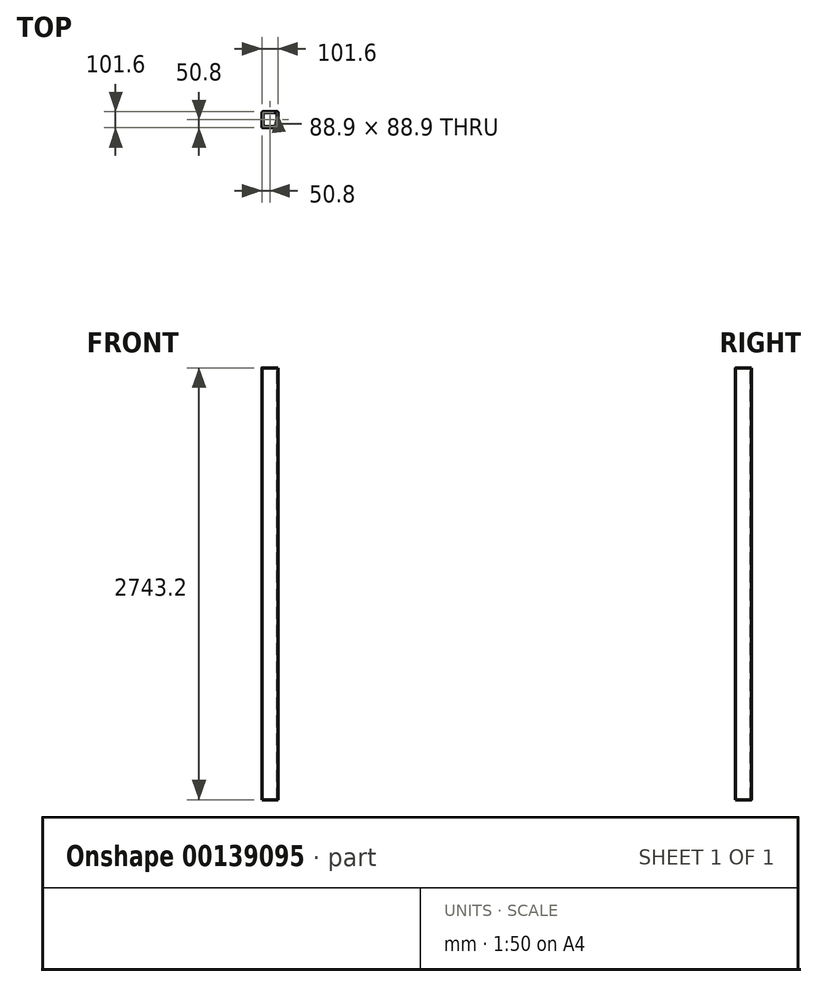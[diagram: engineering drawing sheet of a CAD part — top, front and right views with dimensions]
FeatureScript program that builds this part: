
annotation { "Feature Type Name" : "Feature", "Feature Type Description" : "" }
export const myFeature = defineFeature(function(context is Context, id is Id, definition is map)
    precondition{}
    {
        {
            var Q0;
            Q0=qCreatedBy(makeId("Top.planeOp"),FACE);
            var sketch = newSketch(context, id + "F0", { "sketchPlane" : qUnion([Q0])});
            skLineSegment(sketch, "E0.bottom", {"start": v(50.8, 50.8) * mm, "end": v(-50.8, 50.8) * mm});
            skLineSegment(sketch, "E0.top", {"start": v(50.8, -50.8) * mm, "end": v(-50.8, -50.8) * mm});
            skLineSegment(sketch, "E0.left", {"start": v(50.8, 50.8) * mm, "end": v(50.8, -50.8) * mm});
            skLineSegment(sketch, "E0.right", {"start": v(-50.8, 50.8) * mm, "end": v(-50.8, -50.8) * mm});
            skPoint(sketch, "E0.middle", {"position": v(0, 0) * mm});
            skSolve(sketch);
        }
        {
            var Q0;
            Q0 = qSketchRegion(id + "F0", true);
            extrude(context, id + "F1", {"entities" : qUnion([Q0]), "depth" : 2743.2 * mm});
        }
        {
            var Q0;
            Q0=makeQuery(id+"F1.opExtrude","CAP_FACE",FACE,{"disambiguationData":[OSD([sQuery(id+"F0.wireOp",EDGE,"E0.bottom"),sQuery(id+"F0.wireOp",EDGE,"E0.top"),sQuery(id+"F0.wireOp",EDGE,"E0.left"),sQuery(id+"F0.wireOp",EDGE,"E0.right")])],"isStart":false});
            var sketch = newSketch(context, id + "F2", { "sketchPlane" : qUnion([Q0])});
            skLineSegment(sketch, "E1.bottom", {"start": v(44.45, 44.45) * mm, "end": v(-44.45, 44.45) * mm});
            skLineSegment(sketch, "E1.top", {"start": v(44.45, -44.45) * mm, "end": v(-44.45, -44.45) * mm});
            skLineSegment(sketch, "E1.left", {"start": v(44.45, 44.45) * mm, "end": v(44.45, -44.45) * mm});
            skLineSegment(sketch, "E1.right", {"start": v(-44.45, 44.45) * mm, "end": v(-44.45, -44.45) * mm});
            skPoint(sketch, "E1.middle", {"position": v(0, 0) * mm});
            skSolve(sketch);
        }
        {
            var Q0;
            Q0 = qSketchRegion(id + "F2", true);
            extrude(context, id + "F3", {"entities" : qUnion([Q0]), "operationType" : NewBodyOperationType.REMOVE, "endBound" : BoundingType.THROUGH_ALL, "oppositeDirection" : true, "depth" : 25.4 * mm});
        }
        {
            var Q0;
            Q0=makeQuery(id+"F1.opExtrude","SWEPT_EDGE",EDGE,{"disambiguationData":[OSD([sQuery(id+"F0.wireOp",EDGE,"E0.top"),sQuery(id+"F0.wireOp",EDGE,"E0.left")])]});
            var Q1;
            Q1=makeQuery(id+"F1.opExtrude","SWEPT_EDGE",EDGE,{"disambiguationData":[OSD([sQuery(id+"F0.wireOp",EDGE,"E0.bottom"),sQuery(id+"F0.wireOp",EDGE,"E0.left")])]});
            var Q2;
            Q2=makeQuery(id+"F1.opExtrude","SWEPT_EDGE",EDGE,{"disambiguationData":[OSD([sQuery(id+"F0.wireOp",EDGE,"E0.top"),sQuery(id+"F0.wireOp",EDGE,"E0.right")])]});
            var Q3;
            Q3=makeQuery(id+"F1.opExtrude","SWEPT_EDGE",EDGE,{"disambiguationData":[OSD([sQuery(id+"F0.wireOp",EDGE,"E0.bottom"),sQuery(id+"F0.wireOp",EDGE,"E0.right")])]});
            fillet(context, id + "F4", {"entities" : qUnion([Q0, Q1, Q2, Q3]), "radius" : 5.08 * mm, "tangentPropagation" : true, "allowEdgeOverflow" : false});
        }
    });
